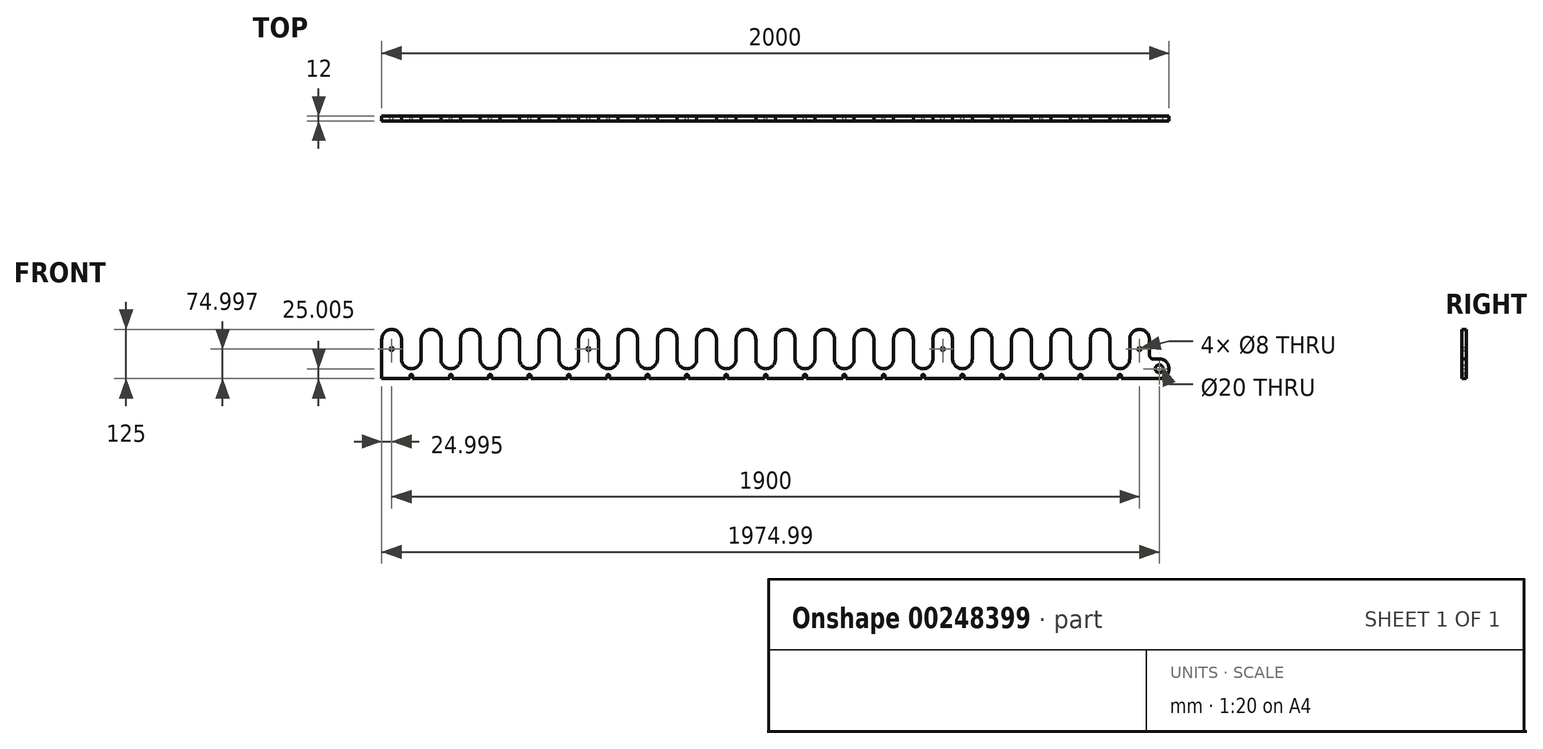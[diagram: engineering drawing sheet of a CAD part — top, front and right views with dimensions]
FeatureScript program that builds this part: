
annotation { "Feature Type Name" : "Feature", "Feature Type Description" : "" }
export const myFeature = defineFeature(function(context is Context, id is Id, definition is map)
    precondition{}
    {
        {
            var Q0;
            Q0=qCreatedBy(makeId("Front.planeOp"),FACE);
            var sketch = newSketch(context, id + "F0", { "sketchPlane" : qUnion([Q0])});
            skLineSegment(sketch, "E0.top", {"start": v(-29.58, -70.67) * mm, "end": v(20.42, -70.67) * mm});
            skLineSegment(sketch, "E0.left", {"start": v(-29.58, 29.33) * mm, "end": v(-29.58, -70.67) * mm});
            skLineSegment(sketch, "E0.right", {"start": v(20.42, 29.33) * mm, "end": v(20.42, -20.67) * mm});
            skArc(sketch, "E1", {"start": v(-29.58, 29.33) * mm, "mid": v(-4.58, 54.33) * mm, "end": v(20.42, 29.33) * mm});
            skLineSegment(sketch, "E2.bottom", {"start": v(20.42, -70.67) * mm, "end": v(42.03, -70.67) * mm});
            skArc(sketch, "E3.MirrorCS", {"start": v(20.42, -20.67) * mm, "mid": v(45.42, -45.67) * mm, "end": v(70.42, -20.67) * mm});
            skArc(sketch, "E4", {"start": v(49.03, -63.36) * mm, "mid": v(45.53, -59.86) * mm, "end": v(42.03, -63.36) * mm});
            skLineSegment(sketch, "E5.left", {"start": v(49.03, -63.36) * mm, "end": v(49.03, -70.67) * mm});
            skLineSegment(sketch, "E5.right", {"start": v(42.03, -63.36) * mm, "end": v(42.03, -70.67) * mm});
            skLineSegment(sketch, "E6.trimOffspring", {"start": v(49.03, -70.67) * mm, "end": v(70.42, -70.67) * mm});
            skLineSegment(sketch, "E7", {"start": v(70.42, -20.67) * mm, "end": v(70.42, 29.33) * mm});
            skArc(sketch, "E8.1.0.0", {"start": v(70.42, 29.33) * mm, "mid": v(95.42, 54.33) * mm, "end": v(120.42, 29.33) * mm});
            skLineSegment(sketch, "E8.1.0.1", {"start": v(70.42, -70.67) * mm, "end": v(120.42, -70.67) * mm});
            skLineSegment(sketch, "E8.1.0.2", {"start": v(120.42, -70.67) * mm, "end": v(142.03, -70.67) * mm});
            skLineSegment(sketch, "E8.1.0.3", {"start": v(142.03, -63.36) * mm, "end": v(142.03, -70.67) * mm});
            skArc(sketch, "E8.1.0.4", {"start": v(149.03, -63.36) * mm, "mid": v(145.53, -59.86) * mm, "end": v(142.03, -63.36) * mm});
            skLineSegment(sketch, "E8.1.0.5", {"start": v(149.03, -63.36) * mm, "end": v(149.03, -70.67) * mm});
            skLineSegment(sketch, "E8.1.0.6", {"start": v(149.03, -70.67) * mm, "end": v(170.42, -70.67) * mm});
            skLineSegment(sketch, "E8.1.0.7", {"start": v(120.42, 29.33) * mm, "end": v(120.42, -20.67) * mm});
            skArc(sketch, "E8.1.0.8", {"start": v(120.42, -20.67) * mm, "mid": v(145.42, -45.67) * mm, "end": v(170.42, -20.67) * mm});
            skLineSegment(sketch, "E8.1.0.9", {"start": v(170.42, -20.67) * mm, "end": v(170.42, 29.33) * mm});
            skArc(sketch, "E8.2.0.0", {"start": v(170.42, 29.33) * mm, "mid": v(195.42, 54.33) * mm, "end": v(220.42, 29.33) * mm});
            skLineSegment(sketch, "E8.2.0.1", {"start": v(170.42, -70.67) * mm, "end": v(220.42, -70.67) * mm});
            skLineSegment(sketch, "E8.2.0.2", {"start": v(220.42, -70.67) * mm, "end": v(242.03, -70.67) * mm});
            skLineSegment(sketch, "E8.2.0.3", {"start": v(242.03, -63.36) * mm, "end": v(242.03, -70.67) * mm});
            skArc(sketch, "E8.2.0.4", {"start": v(249.03, -63.36) * mm, "mid": v(245.53, -59.86) * mm, "end": v(242.03, -63.36) * mm});
            skLineSegment(sketch, "E8.2.0.5", {"start": v(249.03, -63.36) * mm, "end": v(249.03, -70.67) * mm});
            skLineSegment(sketch, "E8.2.0.6", {"start": v(249.03, -70.67) * mm, "end": v(270.42, -70.67) * mm});
            skLineSegment(sketch, "E8.2.0.7", {"start": v(220.42, 29.33) * mm, "end": v(220.42, -20.67) * mm});
            skArc(sketch, "E8.2.0.8", {"start": v(220.42, -20.67) * mm, "mid": v(245.42, -45.67) * mm, "end": v(270.42, -20.67) * mm});
            skLineSegment(sketch, "E8.2.0.9", {"start": v(270.42, -20.67) * mm, "end": v(270.42, 29.33) * mm});
            skArc(sketch, "E8.3.0.0", {"start": v(270.42, 29.33) * mm, "mid": v(295.42, 54.33) * mm, "end": v(320.42, 29.33) * mm});
            skLineSegment(sketch, "E8.3.0.1", {"start": v(270.42, -70.67) * mm, "end": v(320.42, -70.67) * mm});
            skLineSegment(sketch, "E8.3.0.2", {"start": v(320.42, -70.67) * mm, "end": v(342.03, -70.67) * mm});
            skLineSegment(sketch, "E8.3.0.3", {"start": v(342.03, -63.36) * mm, "end": v(342.03, -70.67) * mm});
            skArc(sketch, "E8.3.0.4", {"start": v(349.03, -63.36) * mm, "mid": v(345.53, -59.86) * mm, "end": v(342.03, -63.36) * mm});
            skLineSegment(sketch, "E8.3.0.5", {"start": v(349.03, -63.36) * mm, "end": v(349.03, -70.67) * mm});
            skLineSegment(sketch, "E8.3.0.6", {"start": v(349.03, -70.67) * mm, "end": v(370.42, -70.67) * mm});
            skLineSegment(sketch, "E8.3.0.7", {"start": v(320.42, 29.33) * mm, "end": v(320.42, -20.67) * mm});
            skArc(sketch, "E8.3.0.8", {"start": v(320.42, -20.67) * mm, "mid": v(345.42, -45.67) * mm, "end": v(370.42, -20.67) * mm});
            skLineSegment(sketch, "E8.3.0.9", {"start": v(370.42, -20.67) * mm, "end": v(370.42, 29.33) * mm});
            skArc(sketch, "E8.4.0.0", {"start": v(370.42, 29.33) * mm, "mid": v(395.42, 54.33) * mm, "end": v(420.42, 29.33) * mm});
            skLineSegment(sketch, "E8.4.0.1", {"start": v(370.42, -70.67) * mm, "end": v(420.42, -70.67) * mm});
            skLineSegment(sketch, "E8.4.0.2", {"start": v(420.42, -70.67) * mm, "end": v(442.03, -70.67) * mm});
            skLineSegment(sketch, "E8.4.0.3", {"start": v(442.03, -63.36) * mm, "end": v(442.03, -70.67) * mm});
            skArc(sketch, "E8.4.0.4", {"start": v(449.03, -63.36) * mm, "mid": v(445.53, -59.86) * mm, "end": v(442.03, -63.36) * mm});
            skLineSegment(sketch, "E8.4.0.5", {"start": v(449.03, -63.36) * mm, "end": v(449.03, -70.67) * mm});
            skLineSegment(sketch, "E8.4.0.6", {"start": v(449.03, -70.67) * mm, "end": v(470.42, -70.67) * mm});
            skLineSegment(sketch, "E8.4.0.7", {"start": v(420.42, 29.33) * mm, "end": v(420.42, -20.67) * mm});
            skArc(sketch, "E8.4.0.8", {"start": v(420.42, -20.67) * mm, "mid": v(445.42, -45.67) * mm, "end": v(470.42, -20.67) * mm});
            skLineSegment(sketch, "E8.4.0.9", {"start": v(470.42, -20.67) * mm, "end": v(470.42, 29.33) * mm});
            skArc(sketch, "E8.5.0.0", {"start": v(470.42, 29.33) * mm, "mid": v(495.42, 54.33) * mm, "end": v(520.42, 29.33) * mm});
            skLineSegment(sketch, "E8.5.0.1", {"start": v(470.42, -70.67) * mm, "end": v(520.42, -70.67) * mm});
            skLineSegment(sketch, "E8.5.0.2", {"start": v(520.42, -70.67) * mm, "end": v(542.03, -70.67) * mm});
            skLineSegment(sketch, "E8.5.0.3", {"start": v(542.03, -63.36) * mm, "end": v(542.03, -70.67) * mm});
            skArc(sketch, "E8.5.0.4", {"start": v(549.03, -63.36) * mm, "mid": v(545.53, -59.86) * mm, "end": v(542.03, -63.36) * mm});
            skLineSegment(sketch, "E8.5.0.5", {"start": v(549.03, -63.36) * mm, "end": v(549.03, -70.67) * mm});
            skLineSegment(sketch, "E8.5.0.6", {"start": v(549.03, -70.67) * mm, "end": v(570.42, -70.67) * mm});
            skLineSegment(sketch, "E8.5.0.7", {"start": v(520.42, 29.33) * mm, "end": v(520.42, -20.67) * mm});
            skArc(sketch, "E8.5.0.8", {"start": v(520.42, -20.67) * mm, "mid": v(545.42, -45.67) * mm, "end": v(570.42, -20.67) * mm});
            skLineSegment(sketch, "E8.5.0.9", {"start": v(570.42, -20.67) * mm, "end": v(570.42, 29.33) * mm});
            skArc(sketch, "E8.6.0.0", {"start": v(570.42, 29.33) * mm, "mid": v(595.42, 54.33) * mm, "end": v(620.42, 29.33) * mm});
            skLineSegment(sketch, "E8.6.0.1", {"start": v(570.42, -70.67) * mm, "end": v(620.42, -70.67) * mm});
            skLineSegment(sketch, "E8.6.0.2", {"start": v(620.42, -70.67) * mm, "end": v(642.03, -70.67) * mm});
            skLineSegment(sketch, "E8.6.0.3", {"start": v(642.03, -63.36) * mm, "end": v(642.03, -70.67) * mm});
            skArc(sketch, "E8.6.0.4", {"start": v(649.03, -63.36) * mm, "mid": v(645.53, -59.86) * mm, "end": v(642.03, -63.36) * mm});
            skLineSegment(sketch, "E8.6.0.5", {"start": v(649.03, -63.36) * mm, "end": v(649.03, -70.67) * mm});
            skLineSegment(sketch, "E8.6.0.6", {"start": v(649.03, -70.67) * mm, "end": v(670.42, -70.67) * mm});
            skLineSegment(sketch, "E8.6.0.7", {"start": v(620.42, 29.33) * mm, "end": v(620.42, -20.67) * mm});
            skArc(sketch, "E8.6.0.8", {"start": v(620.42, -20.67) * mm, "mid": v(645.42, -45.67) * mm, "end": v(670.42, -20.67) * mm});
            skLineSegment(sketch, "E8.6.0.9", {"start": v(670.42, -20.67) * mm, "end": v(670.42, 29.33) * mm});
            skArc(sketch, "E8.7.0.0", {"start": v(670.42, 29.33) * mm, "mid": v(695.42, 54.33) * mm, "end": v(720.42, 29.33) * mm});
            skLineSegment(sketch, "E8.7.0.1", {"start": v(670.42, -70.67) * mm, "end": v(720.42, -70.67) * mm});
            skLineSegment(sketch, "E8.7.0.2", {"start": v(720.42, -70.67) * mm, "end": v(742.03, -70.67) * mm});
            skLineSegment(sketch, "E8.7.0.3", {"start": v(742.03, -63.36) * mm, "end": v(742.03, -70.67) * mm});
            skArc(sketch, "E8.7.0.4", {"start": v(749.03, -63.36) * mm, "mid": v(745.53, -59.86) * mm, "end": v(742.03, -63.36) * mm});
            skLineSegment(sketch, "E8.7.0.5", {"start": v(749.03, -63.36) * mm, "end": v(749.03, -70.67) * mm});
            skLineSegment(sketch, "E8.7.0.6", {"start": v(749.03, -70.67) * mm, "end": v(770.42, -70.67) * mm});
            skLineSegment(sketch, "E8.7.0.7", {"start": v(720.42, 29.33) * mm, "end": v(720.42, -20.67) * mm});
            skArc(sketch, "E8.7.0.8", {"start": v(720.42, -20.67) * mm, "mid": v(745.42, -45.67) * mm, "end": v(770.42, -20.67) * mm});
            skLineSegment(sketch, "E8.7.0.9", {"start": v(770.42, -20.67) * mm, "end": v(770.42, 29.33) * mm});
            skArc(sketch, "E8.8.0.0", {"start": v(770.42, 29.33) * mm, "mid": v(795.42, 54.33) * mm, "end": v(820.42, 29.33) * mm});
            skLineSegment(sketch, "E8.8.0.1", {"start": v(770.42, -70.67) * mm, "end": v(820.42, -70.67) * mm});
            skLineSegment(sketch, "E8.8.0.2", {"start": v(820.42, -70.67) * mm, "end": v(842.03, -70.67) * mm});
            skLineSegment(sketch, "E8.8.0.3", {"start": v(842.03, -63.36) * mm, "end": v(842.03, -70.67) * mm});
            skArc(sketch, "E8.8.0.4", {"start": v(849.03, -63.36) * mm, "mid": v(845.53, -59.86) * mm, "end": v(842.03, -63.36) * mm});
            skLineSegment(sketch, "E8.8.0.5", {"start": v(849.03, -63.36) * mm, "end": v(849.03, -70.67) * mm});
            skLineSegment(sketch, "E8.8.0.6", {"start": v(849.03, -70.67) * mm, "end": v(870.42, -70.67) * mm});
            skLineSegment(sketch, "E8.8.0.7", {"start": v(820.42, 29.33) * mm, "end": v(820.42, -20.67) * mm});
            skArc(sketch, "E8.8.0.8", {"start": v(820.42, -20.67) * mm, "mid": v(845.42, -45.67) * mm, "end": v(870.42, -20.67) * mm});
            skLineSegment(sketch, "E8.8.0.9", {"start": v(870.42, -20.67) * mm, "end": v(870.42, 29.33) * mm});
            skArc(sketch, "E8.9.0.0", {"start": v(870.42, 29.33) * mm, "mid": v(895.42, 54.33) * mm, "end": v(920.42, 29.33) * mm});
            skLineSegment(sketch, "E8.9.0.1", {"start": v(870.42, -70.67) * mm, "end": v(920.42, -70.67) * mm});
            skLineSegment(sketch, "E8.9.0.2", {"start": v(920.42, -70.67) * mm, "end": v(942.03, -70.67) * mm});
            skLineSegment(sketch, "E8.9.0.3", {"start": v(942.03, -63.36) * mm, "end": v(942.03, -70.67) * mm});
            skArc(sketch, "E8.9.0.4", {"start": v(949.03, -63.36) * mm, "mid": v(945.53, -59.86) * mm, "end": v(942.03, -63.36) * mm});
            skLineSegment(sketch, "E8.9.0.5", {"start": v(949.03, -63.36) * mm, "end": v(949.03, -70.67) * mm});
            skLineSegment(sketch, "E8.9.0.6", {"start": v(949.03, -70.67) * mm, "end": v(970.42, -70.67) * mm});
            skLineSegment(sketch, "E8.9.0.7", {"start": v(920.42, 29.33) * mm, "end": v(920.42, -20.67) * mm});
            skArc(sketch, "E8.9.0.8", {"start": v(920.42, -20.67) * mm, "mid": v(945.42, -45.67) * mm, "end": v(970.42, -20.67) * mm});
            skLineSegment(sketch, "E8.9.0.9", {"start": v(970.42, -20.67) * mm, "end": v(970.42, 29.33) * mm});
            skArc(sketch, "E8.10.0.0", {"start": v(970.42, 29.33) * mm, "mid": v(995.42, 54.33) * mm, "end": v(1020.42, 29.33) * mm});
            skLineSegment(sketch, "E8.10.0.1", {"start": v(970.42, -70.67) * mm, "end": v(1020.42, -70.67) * mm});
            skLineSegment(sketch, "E8.10.0.2", {"start": v(1020.42, -70.67) * mm, "end": v(1042.03, -70.67) * mm});
            skLineSegment(sketch, "E8.10.0.3", {"start": v(1042.03, -63.36) * mm, "end": v(1042.03, -70.67) * mm});
            skArc(sketch, "E8.10.0.4", {"start": v(1049.03, -63.36) * mm, "mid": v(1045.53, -59.86) * mm, "end": v(1042.03, -63.36) * mm});
            skLineSegment(sketch, "E8.10.0.5", {"start": v(1049.03, -63.36) * mm, "end": v(1049.03, -70.67) * mm});
            skLineSegment(sketch, "E8.10.0.6", {"start": v(1049.03, -70.67) * mm, "end": v(1070.42, -70.67) * mm});
            skLineSegment(sketch, "E8.10.0.7", {"start": v(1020.42, 29.33) * mm, "end": v(1020.42, -20.67) * mm});
            skArc(sketch, "E8.10.0.8", {"start": v(1020.42, -20.67) * mm, "mid": v(1045.42, -45.67) * mm, "end": v(1070.42, -20.67) * mm});
            skLineSegment(sketch, "E8.10.0.9", {"start": v(1070.42, -20.67) * mm, "end": v(1070.42, 29.33) * mm});
            skArc(sketch, "E8.11.0.0", {"start": v(1070.42, 29.33) * mm, "mid": v(1095.42, 54.33) * mm, "end": v(1120.42, 29.33) * mm});
            skLineSegment(sketch, "E8.11.0.1", {"start": v(1070.42, -70.67) * mm, "end": v(1120.42, -70.67) * mm});
            skLineSegment(sketch, "E8.11.0.2", {"start": v(1120.42, -70.67) * mm, "end": v(1142.03, -70.67) * mm});
            skLineSegment(sketch, "E8.11.0.3", {"start": v(1142.03, -63.36) * mm, "end": v(1142.03, -70.67) * mm});
            skArc(sketch, "E8.11.0.4", {"start": v(1149.03, -63.36) * mm, "mid": v(1145.53, -59.86) * mm, "end": v(1142.03, -63.36) * mm});
            skLineSegment(sketch, "E8.11.0.5", {"start": v(1149.03, -63.36) * mm, "end": v(1149.03, -70.67) * mm});
            skLineSegment(sketch, "E8.11.0.6", {"start": v(1149.03, -70.67) * mm, "end": v(1170.42, -70.67) * mm});
            skLineSegment(sketch, "E8.11.0.7", {"start": v(1120.42, 29.33) * mm, "end": v(1120.42, -20.67) * mm});
            skArc(sketch, "E8.11.0.8", {"start": v(1120.42, -20.67) * mm, "mid": v(1145.42, -45.67) * mm, "end": v(1170.42, -20.67) * mm});
            skLineSegment(sketch, "E8.11.0.9", {"start": v(1170.42, -20.67) * mm, "end": v(1170.42, 29.33) * mm});
            skArc(sketch, "E8.12.0.0", {"start": v(1170.42, 29.33) * mm, "mid": v(1195.42, 54.33) * mm, "end": v(1220.42, 29.33) * mm});
            skLineSegment(sketch, "E8.12.0.1", {"start": v(1170.42, -70.67) * mm, "end": v(1220.42, -70.67) * mm});
            skLineSegment(sketch, "E8.12.0.2", {"start": v(1220.42, -70.67) * mm, "end": v(1242.03, -70.67) * mm});
            skLineSegment(sketch, "E8.12.0.3", {"start": v(1242.03, -63.36) * mm, "end": v(1242.03, -70.67) * mm});
            skArc(sketch, "E8.12.0.4", {"start": v(1249.03, -63.36) * mm, "mid": v(1245.53, -59.86) * mm, "end": v(1242.03, -63.36) * mm});
            skLineSegment(sketch, "E8.12.0.5", {"start": v(1249.03, -63.36) * mm, "end": v(1249.03, -70.67) * mm});
            skLineSegment(sketch, "E8.12.0.6", {"start": v(1249.03, -70.67) * mm, "end": v(1270.42, -70.67) * mm});
            skLineSegment(sketch, "E8.12.0.7", {"start": v(1220.42, 29.33) * mm, "end": v(1220.42, -20.67) * mm});
            skArc(sketch, "E8.12.0.8", {"start": v(1220.42, -20.67) * mm, "mid": v(1245.42, -45.67) * mm, "end": v(1270.42, -20.67) * mm});
            skLineSegment(sketch, "E8.12.0.9", {"start": v(1270.42, -20.67) * mm, "end": v(1270.42, 29.33) * mm});
            skArc(sketch, "E8.13.0.0", {"start": v(1270.42, 29.33) * mm, "mid": v(1295.42, 54.33) * mm, "end": v(1320.42, 29.33) * mm});
            skLineSegment(sketch, "E8.13.0.1", {"start": v(1270.42, -70.67) * mm, "end": v(1320.42, -70.67) * mm});
            skLineSegment(sketch, "E8.13.0.2", {"start": v(1320.42, -70.67) * mm, "end": v(1342.03, -70.67) * mm});
            skLineSegment(sketch, "E8.13.0.3", {"start": v(1342.03, -63.36) * mm, "end": v(1342.03, -70.67) * mm});
            skArc(sketch, "E8.13.0.4", {"start": v(1349.03, -63.36) * mm, "mid": v(1345.53, -59.86) * mm, "end": v(1342.03, -63.36) * mm});
            skLineSegment(sketch, "E8.13.0.5", {"start": v(1349.03, -63.36) * mm, "end": v(1349.03, -70.67) * mm});
            skLineSegment(sketch, "E8.13.0.6", {"start": v(1349.03, -70.67) * mm, "end": v(1370.42, -70.67) * mm});
            skLineSegment(sketch, "E8.13.0.7", {"start": v(1320.42, 29.33) * mm, "end": v(1320.42, -20.67) * mm});
            skArc(sketch, "E8.13.0.8", {"start": v(1320.42, -20.67) * mm, "mid": v(1345.42, -45.67) * mm, "end": v(1370.42, -20.67) * mm});
            skLineSegment(sketch, "E8.13.0.9", {"start": v(1370.42, -20.67) * mm, "end": v(1370.42, 29.33) * mm});
            skArc(sketch, "E8.14.0.0", {"start": v(1370.42, 29.33) * mm, "mid": v(1395.42, 54.33) * mm, "end": v(1420.42, 29.33) * mm});
            skLineSegment(sketch, "E8.14.0.1", {"start": v(1370.42, -70.67) * mm, "end": v(1420.42, -70.67) * mm});
            skLineSegment(sketch, "E8.14.0.2", {"start": v(1420.42, -70.67) * mm, "end": v(1442.03, -70.67) * mm});
            skLineSegment(sketch, "E8.14.0.3", {"start": v(1442.03, -63.36) * mm, "end": v(1442.03, -70.67) * mm});
            skArc(sketch, "E8.14.0.4", {"start": v(1449.03, -63.36) * mm, "mid": v(1445.53, -59.86) * mm, "end": v(1442.03, -63.36) * mm});
            skLineSegment(sketch, "E8.14.0.5", {"start": v(1449.03, -63.36) * mm, "end": v(1449.03, -70.67) * mm});
            skLineSegment(sketch, "E8.14.0.6", {"start": v(1449.03, -70.67) * mm, "end": v(1470.42, -70.67) * mm});
            skLineSegment(sketch, "E8.14.0.7", {"start": v(1420.42, 29.33) * mm, "end": v(1420.42, -20.67) * mm});
            skArc(sketch, "E8.14.0.8", {"start": v(1420.42, -20.67) * mm, "mid": v(1445.42, -45.67) * mm, "end": v(1470.42, -20.67) * mm});
            skLineSegment(sketch, "E8.14.0.9", {"start": v(1470.42, -20.67) * mm, "end": v(1470.42, 29.33) * mm});
            skArc(sketch, "E8.15.0.0", {"start": v(1470.42, 29.33) * mm, "mid": v(1495.42, 54.33) * mm, "end": v(1520.42, 29.33) * mm});
            skLineSegment(sketch, "E8.15.0.1", {"start": v(1470.42, -70.67) * mm, "end": v(1520.42, -70.67) * mm});
            skLineSegment(sketch, "E8.15.0.2", {"start": v(1520.42, -70.67) * mm, "end": v(1542.03, -70.67) * mm});
            skLineSegment(sketch, "E8.15.0.3", {"start": v(1542.03, -63.36) * mm, "end": v(1542.03, -70.67) * mm});
            skArc(sketch, "E8.15.0.4", {"start": v(1549.03, -63.36) * mm, "mid": v(1545.53, -59.86) * mm, "end": v(1542.03, -63.36) * mm});
            skLineSegment(sketch, "E8.15.0.5", {"start": v(1549.03, -63.36) * mm, "end": v(1549.03, -70.67) * mm});
            skLineSegment(sketch, "E8.15.0.6", {"start": v(1549.03, -70.67) * mm, "end": v(1570.42, -70.67) * mm});
            skLineSegment(sketch, "E8.15.0.7", {"start": v(1520.42, 29.33) * mm, "end": v(1520.42, -20.67) * mm});
            skArc(sketch, "E8.15.0.8", {"start": v(1520.42, -20.67) * mm, "mid": v(1545.42, -45.67) * mm, "end": v(1570.42, -20.67) * mm});
            skLineSegment(sketch, "E8.15.0.9", {"start": v(1570.42, -20.67) * mm, "end": v(1570.42, 29.33) * mm});
            skArc(sketch, "E8.16.0.0", {"start": v(1570.42, 29.33) * mm, "mid": v(1595.42, 54.33) * mm, "end": v(1620.42, 29.33) * mm});
            skLineSegment(sketch, "E8.16.0.1", {"start": v(1570.42, -70.67) * mm, "end": v(1620.42, -70.67) * mm});
            skLineSegment(sketch, "E8.16.0.2", {"start": v(1620.42, -70.67) * mm, "end": v(1642.03, -70.67) * mm});
            skLineSegment(sketch, "E8.16.0.3", {"start": v(1642.03, -63.36) * mm, "end": v(1642.03, -70.67) * mm});
            skArc(sketch, "E8.16.0.4", {"start": v(1649.03, -63.36) * mm, "mid": v(1645.53, -59.86) * mm, "end": v(1642.03, -63.36) * mm});
            skLineSegment(sketch, "E8.16.0.5", {"start": v(1649.03, -63.36) * mm, "end": v(1649.03, -70.67) * mm});
            skLineSegment(sketch, "E8.16.0.6", {"start": v(1649.03, -70.67) * mm, "end": v(1670.42, -70.67) * mm});
            skLineSegment(sketch, "E8.16.0.7", {"start": v(1620.42, 29.33) * mm, "end": v(1620.42, -20.67) * mm});
            skArc(sketch, "E8.16.0.8", {"start": v(1620.42, -20.67) * mm, "mid": v(1645.42, -45.67) * mm, "end": v(1670.42, -20.67) * mm});
            skLineSegment(sketch, "E8.16.0.9", {"start": v(1670.42, -20.67) * mm, "end": v(1670.42, 29.33) * mm});
            skArc(sketch, "E8.17.0.0", {"start": v(1670.42, 29.33) * mm, "mid": v(1695.42, 54.33) * mm, "end": v(1720.42, 29.33) * mm});
            skLineSegment(sketch, "E8.17.0.1", {"start": v(1670.42, -70.67) * mm, "end": v(1720.42, -70.67) * mm});
            skLineSegment(sketch, "E8.17.0.2", {"start": v(1720.42, -70.67) * mm, "end": v(1742.03, -70.67) * mm});
            skLineSegment(sketch, "E8.17.0.3", {"start": v(1742.03, -63.36) * mm, "end": v(1742.03, -70.67) * mm});
            skArc(sketch, "E8.17.0.4", {"start": v(1749.03, -63.36) * mm, "mid": v(1745.53, -59.86) * mm, "end": v(1742.03, -63.36) * mm});
            skLineSegment(sketch, "E8.17.0.5", {"start": v(1749.03, -63.36) * mm, "end": v(1749.03, -70.67) * mm});
            skLineSegment(sketch, "E8.17.0.6", {"start": v(1749.03, -70.67) * mm, "end": v(1770.42, -70.67) * mm});
            skLineSegment(sketch, "E8.17.0.7", {"start": v(1720.42, 29.33) * mm, "end": v(1720.42, -20.67) * mm});
            skArc(sketch, "E8.17.0.8", {"start": v(1720.42, -20.67) * mm, "mid": v(1745.42, -45.67) * mm, "end": v(1770.42, -20.67) * mm});
            skLineSegment(sketch, "E8.17.0.9", {"start": v(1770.42, -20.67) * mm, "end": v(1770.42, 29.33) * mm});
            skArc(sketch, "E8.18.0.0", {"start": v(1770.42, 29.33) * mm, "mid": v(1795.42, 54.33) * mm, "end": v(1820.42, 29.33) * mm});
            skLineSegment(sketch, "E8.18.0.1", {"start": v(1770.42, -70.67) * mm, "end": v(1820.42, -70.67) * mm});
            skLineSegment(sketch, "E8.18.0.2", {"start": v(1820.42, -70.67) * mm, "end": v(1842.03, -70.67) * mm});
            skLineSegment(sketch, "E8.18.0.3", {"start": v(1842.03, -63.36) * mm, "end": v(1842.03, -70.67) * mm});
            skArc(sketch, "E8.18.0.4", {"start": v(1849.03, -63.36) * mm, "mid": v(1845.53, -59.86) * mm, "end": v(1842.03, -63.36) * mm});
            skLineSegment(sketch, "E8.18.0.5", {"start": v(1849.03, -63.36) * mm, "end": v(1849.03, -70.67) * mm});
            skLineSegment(sketch, "E8.18.0.6", {"start": v(1849.03, -70.67) * mm, "end": v(1870.42, -70.67) * mm});
            skLineSegment(sketch, "E8.18.0.7", {"start": v(1820.42, 29.33) * mm, "end": v(1820.42, -20.67) * mm});
            skArc(sketch, "E8.18.0.8", {"start": v(1820.42, -20.67) * mm, "mid": v(1845.42, -45.67) * mm, "end": v(1870.42, -20.67) * mm});
            skLineSegment(sketch, "E8.18.0.9", {"start": v(1870.42, -20.67) * mm, "end": v(1870.42, 29.33) * mm});
            skArc(sketch, "E8.19.0.0", {"start": v(1870.42, 29.33) * mm, "mid": v(1895.42, 54.33) * mm, "end": v(1920.42, 29.33) * mm});
            skLineSegment(sketch, "E8.19.0.1", {"start": v(1870.42, -70.67) * mm, "end": v(1920.42, -70.67) * mm});
            skLineSegment(sketch, "E8.19.0.7", {"start": v(1920.42, 29.33) * mm, "end": v(1920.42, -10.66) * mm});
            skLineSegment(sketch, "E8.direction1", {"start": v(-29.58, -70.67) * mm, "end": v(70.42, -70.67) * mm, "construction": true});
            skLineSegment(sketch, "E9", {"start": v(1930.42, -20.66) * mm, "end": v(1945.42, -20.66) * mm});
            skLineSegment(sketch, "E10", {"start": v(1920.42, -70.67) * mm, "end": v(1945.42, -70.67) * mm});
            skArc(sketch, "E11", {"start": v(1945.42, -20.66) * mm, "mid": v(1970.42, -45.67) * mm, "end": v(1945.42, -70.67) * mm});
            skPoint(sketch, "E12.visualSharp", {"position": v(1920.42, -20.66) * mm});
            skArc(sketch, "E12.filletArc", {"start": v(1920.42, -10.66) * mm, "mid": v(1923.34, -17.73) * mm, "end": v(1930.42, -20.66) * mm});
            skCircle(sketch, "E13", {"center": v(1945.42, -45.67) * mm, "radius": 10 * mm});
            skLineSegment(sketch, "E14", {"start": v(1895.42, -70.67) * mm, "end": v(1895.42, 4.33) * mm, "construction": true});
            skCircle(sketch, "E15", {"center": v(1895.42, 4.33) * mm, "radius": 4 * mm});
            skCircle(sketch, "E16.1.0.0", {"center": v(1395.42, 4.33) * mm, "radius": 4 * mm});
            skLineSegment(sketch, "E16.direction1", {"start": v(1895.42, 4.33) * mm, "end": v(1395.42, 4.33) * mm, "construction": true});
            skCircle(sketch, "E17.1.0.0", {"center": v(-4.58, 4.33) * mm, "radius": 4 * mm});
            skLineSegment(sketch, "E17.direction1", {"start": v(1895.42, 4.33) * mm, "end": v(-4.58, 4.33) * mm, "construction": true});
            skCircle(sketch, "E18.1.0.0", {"center": v(495.42, 4.33) * mm, "radius": 4 * mm});
            skLineSegment(sketch, "E18.direction1", {"start": v(1895.42, 4.33) * mm, "end": v(495.42, 4.33) * mm, "construction": true});
            skSolve(sketch);
        }
        {
            var Q0;
            Q0=makeQuery(id+"F0.imprint","IMPRINT",FACE,{"disambiguationData":[TD([[makeQuery(id+"F0.imprint","IMPRINT",EDGE,{"derivedFrom":sQuery(id+"F0.wireOp",EDGE,"E0.top")}),1.0]])]});
            extrude(context, id + "F1", {"entities" : qUnion([Q0]), "depth" : 12 * mm});
        }
    });
